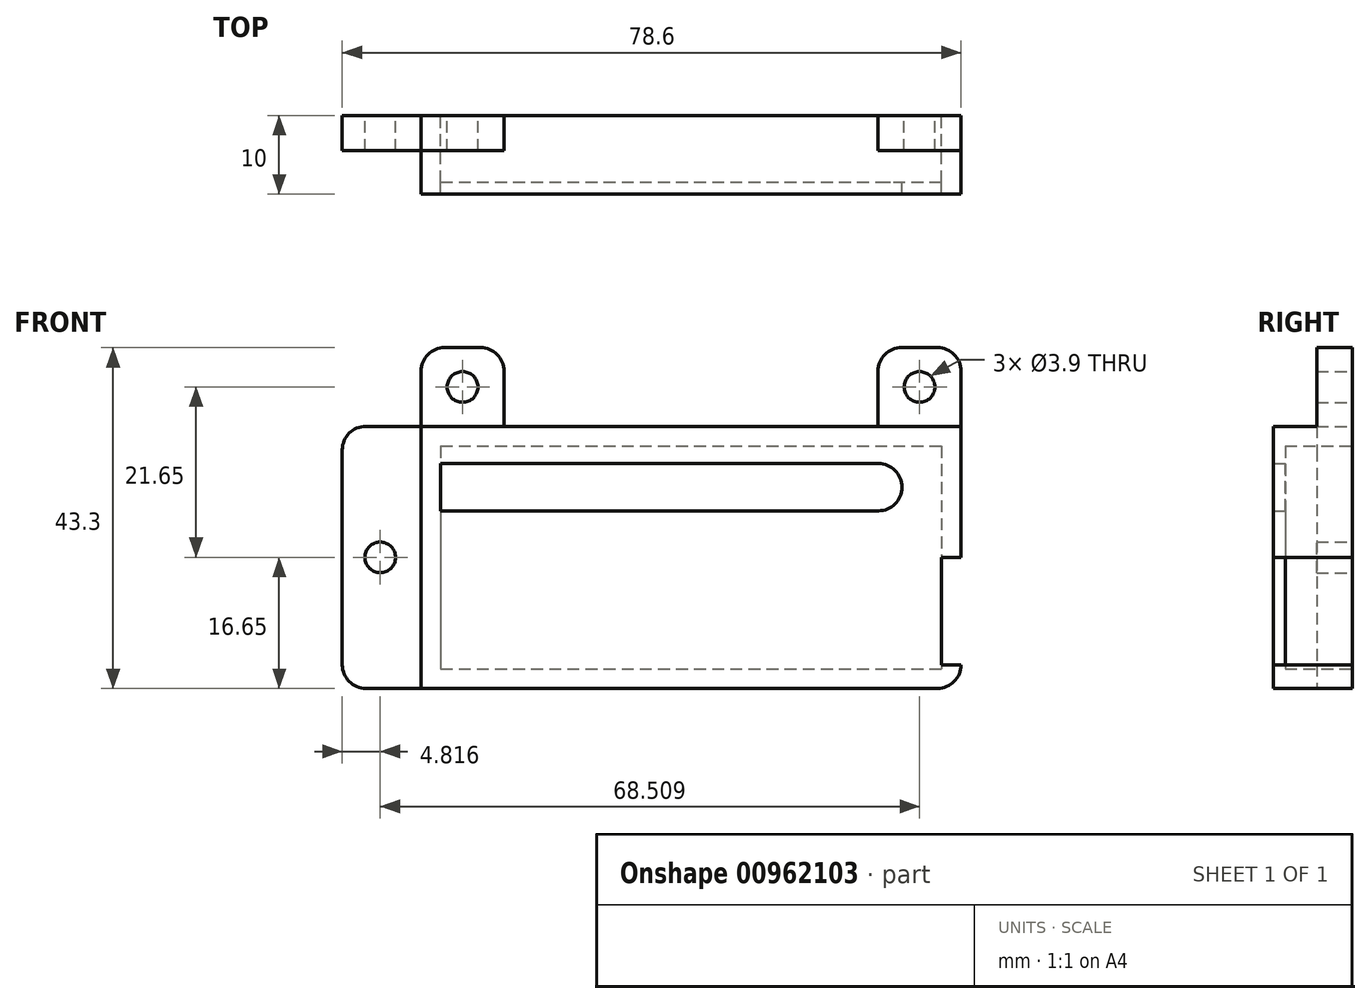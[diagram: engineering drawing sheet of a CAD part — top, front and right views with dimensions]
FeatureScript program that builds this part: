
annotation { "Feature Type Name" : "Feature", "Feature Type Description" : "" }
export const myFeature = defineFeature(function(context is Context, id is Id, definition is map)
    precondition{}
    {
        {
            var Q0;
            Q0=qCreatedBy(makeId("Front.planeOp"),FACE);
            var sketch = newSketch(context, id + "F0", { "sketchPlane" : qUnion([Q0])});
            skLineSegment(sketch, "E0.bottom", {"start": v(-31.8, 14.15) * mm, "end": v(31.8, 14.15) * mm});
            skLineSegment(sketch, "E0.top", {"start": v(-31.8, -14.15) * mm, "end": v(31.8, -14.15) * mm});
            skLineSegment(sketch, "E0.left", {"start": v(-31.8, 14.15) * mm, "end": v(-31.8, -14.15) * mm});
            skLineSegment(sketch, "E0.right", {"start": v(31.8, 14.15) * mm, "end": v(31.8, -14.15) * mm});
            skLineSegment(sketch, "E1", {"start": v(0, 0) * mm, "end": v(0, 14.15) * mm, "construction": true});
            skLineSegment(sketch, "E2", {"start": v(0, 0) * mm, "end": v(0, -14.15) * mm, "construction": true});
            skLineSegment(sketch, "E3", {"start": v(0, 0) * mm, "end": v(31.8, 0) * mm, "construction": true});
            skLineSegment(sketch, "E4", {"start": v(0, 0) * mm, "end": v(-31.8, 0) * mm, "construction": true});
            skLineSegment(sketch, "E5.0", {"start": v(-34.3, 16.65) * mm, "end": v(34.3, 16.65) * mm});
            skLineSegment(sketch, "E5.1", {"start": v(-34.3, 16.65) * mm, "end": v(-34.3, -16.65) * mm});
            skLineSegment(sketch, "E5.2", {"start": v(-34.3, -16.65) * mm, "end": v(31.3, -16.65) * mm});
            skLineSegment(sketch, "E5.3", {"start": v(34.3, 16.65) * mm, "end": v(34.3, 0) * mm});
            skLineSegment(sketch, "E6", {"start": v(23.75, 16.65) * mm, "end": v(23.75, 23.65) * mm});
            skLineSegment(sketch, "E7", {"start": v(26.75, 26.65) * mm, "end": v(31.3, 26.65) * mm});
            skLineSegment(sketch, "E8", {"start": v(34.3, 23.65) * mm, "end": v(34.3, 16.65) * mm});
            skCircle(sketch, "E9", {"center": v(29.02, 21.65) * mm, "radius": 1.95 * mm});
            skLineSegment(sketch, "E10", {"start": v(29.02, 21.65) * mm, "end": v(34.3, 21.65) * mm, "construction": true});
            skLineSegment(sketch, "E11", {"start": v(29.02, 21.65) * mm, "end": v(23.75, 21.65) * mm, "construction": true});
            skLineSegment(sketch, "E12", {"start": v(29.02, 21.65) * mm, "end": v(29.02, 16.65) * mm, "construction": true});
            skLineSegment(sketch, "E13", {"start": v(29.02, 21.65) * mm, "end": v(29.02, 26.65) * mm, "construction": true});
            skLineSegment(sketch, "E14.MirrorCS", {"start": v(-34.3, 23.65) * mm, "end": v(-34.3, 16.65) * mm});
            skLineSegment(sketch, "E15.MirrorCS", {"start": v(-26.75, 26.65) * mm, "end": v(-31.3, 26.65) * mm});
            skLineSegment(sketch, "E16.MirrorCS", {"start": v(-23.75, 16.65) * mm, "end": v(-23.75, 23.65) * mm});
            skCircle(sketch, "E17.MirrorC", {"center": v(-29.02, 21.65) * mm, "radius": 1.95 * mm});
            skLineSegment(sketch, "E18", {"start": v(-34.3, 16.65) * mm, "end": v(-41.3, 16.65) * mm});
            skLineSegment(sketch, "E19", {"start": v(-44.3, 13.65) * mm, "end": v(-44.3, -13.65) * mm});
            skLineSegment(sketch, "E20", {"start": v(-41.3, -16.65) * mm, "end": v(-34.3, -16.65) * mm});
            skCircle(sketch, "E21", {"center": v(-39.48, 0) * mm, "radius": 1.95 * mm});
            skLineSegment(sketch, "E22", {"start": v(34.3, 16.65) * mm, "end": v(41.3, 16.65) * mm});
            skLineSegment(sketch, "E23", {"start": v(44.3, 13.65) * mm, "end": v(44.3, 9.1) * mm});
            skLineSegment(sketch, "E24", {"start": v(41.3, 6.1) * mm, "end": v(34.3, 6.1) * mm});
            skCircle(sketch, "E25", {"center": v(39.3, 11.38) * mm, "radius": 1.95 * mm});
            skLineSegment(sketch, "E26", {"start": v(39.3, 11.38) * mm, "end": v(39.3, 16.65) * mm, "construction": true});
            skLineSegment(sketch, "E27", {"start": v(39.3, 11.38) * mm, "end": v(39.3, 6.1) * mm, "construction": true});
            skLineSegment(sketch, "E28", {"start": v(39.3, 11.38) * mm, "end": v(44.3, 11.38) * mm, "construction": true});
            skLineSegment(sketch, "E29", {"start": v(39.3, 11.38) * mm, "end": v(34.3, 11.38) * mm, "construction": true});
            skLineSegment(sketch, "E30", {"start": v(-31.8, 8.9) * mm, "end": v(23.8, 8.9) * mm, "construction": true});
            skArc(sketch, "E31.0.endCap", {"start": v(23.8, 11.9) * mm, "mid": v(26.8, 8.9) * mm, "end": v(23.8, 5.9) * mm});
            skLineSegment(sketch, "E31.0.left", {"start": v(-31.8, 11.9) * mm, "end": v(23.8, 11.9) * mm});
            skLineSegment(sketch, "E31.0.right", {"start": v(-31.8, 5.9) * mm, "end": v(23.8, 5.9) * mm});
            skLineSegment(sketch, "E32", {"start": v(-31.8, 2.85) * mm, "end": v(31.8, 2.85) * mm, "construction": true});
            skPoint(sketch, "E33.visualSharp", {"position": v(-23.75, 26.65) * mm});
            skArc(sketch, "E33.filletArc", {"start": v(-23.75, 23.65) * mm, "mid": v(-24.63, 25.77) * mm, "end": v(-26.75, 26.65) * mm});
            skPoint(sketch, "E34.visualSharp", {"position": v(-34.3, 26.65) * mm});
            skArc(sketch, "E34.filletArc", {"start": v(-31.3, 26.65) * mm, "mid": v(-33.42, 25.77) * mm, "end": v(-34.3, 23.65) * mm});
            skPoint(sketch, "E35.visualSharp", {"position": v(34.3, 26.65) * mm});
            skArc(sketch, "E35.filletArc", {"start": v(34.3, 23.65) * mm, "mid": v(33.42, 25.77) * mm, "end": v(31.3, 26.65) * mm});
            skPoint(sketch, "E36.visualSharp", {"position": v(23.75, 26.65) * mm});
            skArc(sketch, "E36.filletArc", {"start": v(26.75, 26.65) * mm, "mid": v(24.63, 25.77) * mm, "end": v(23.75, 23.65) * mm});
            skPoint(sketch, "E37.visualSharp", {"position": v(44.3, 16.65) * mm});
            skArc(sketch, "E37.filletArc", {"start": v(44.3, 13.65) * mm, "mid": v(43.42, 15.77) * mm, "end": v(41.3, 16.65) * mm});
            skPoint(sketch, "E38.visualSharp", {"position": v(44.3, 6.1) * mm});
            skArc(sketch, "E38.filletArc", {"start": v(41.3, 6.1) * mm, "mid": v(43.42, 6.98) * mm, "end": v(44.3, 9.1) * mm});
            skPoint(sketch, "E39.visualSharp", {"position": v(-44.3, 16.65) * mm});
            skArc(sketch, "E39.filletArc", {"start": v(-41.3, 16.65) * mm, "mid": v(-43.42, 15.77) * mm, "end": v(-44.3, 13.65) * mm});
            skPoint(sketch, "E40.visualSharp", {"position": v(-44.3, -16.65) * mm});
            skArc(sketch, "E40.filletArc", {"start": v(-44.3, -13.65) * mm, "mid": v(-43.42, -15.77) * mm, "end": v(-41.3, -16.65) * mm});
            skPoint(sketch, "E41.visualSharp", {"position": v(34.3, -16.65) * mm});
            skArc(sketch, "E41.filletArc", {"start": v(31.3, -16.65) * mm, "mid": v(33.42, -15.77) * mm, "end": v(34.3, -13.65) * mm});
            skLineSegment(sketch, "E42", {"start": v(31.8, 0) * mm, "end": v(34.3, 0) * mm});
            skLineSegment(sketch, "E43", {"start": v(34.3, -13.65) * mm, "end": v(31.8, -13.65) * mm});
            skSolve(sketch);
        }
        {
            var Q0;
            {var subQ1=sQuery(id+"F0.wireOp",EDGE,"E14.MirrorCS");Q0=makeQuery(id+"F0.imprint","IMPRINT",FACE,{"disambiguationData":[TD([[makeQuery(id+"F0.imprint","IMPRINT",EDGE,{"derivedFrom":subQ1}),1.0]])]});}
            var Q1;
            {var subQ1=sQuery(id+"F0.wireOp",EDGE,"E6");Q1=makeQuery(id+"F0.imprint","IMPRINT",FACE,{"disambiguationData":[TD([[makeQuery(id+"F0.imprint","IMPRINT",EDGE,{"derivedFrom":subQ1}),-1.0]])]});}
            var Q2;
            {var subQ1=sQuery(id+"F0.wireOp",EDGE,"E22");Q2=makeQuery(id+"F0.imprint","IMPRINT",FACE,{"disambiguationData":[TD([[makeQuery(id+"F0.imprint","IMPRINT",EDGE,{"derivedFrom":subQ1}),-1.0]])]});}
            var Q3;
            {var subQ9=sQuery(id+"F0.wireOp",EDGE,"E0.bottom");Q3=makeQuery(id+"F0.imprint","IMPRINT",FACE,{"disambiguationData":[TD([[makeQuery(id+"F0.imprint","IMPRINT",EDGE,{"derivedFrom":subQ9}),1.0]])]});}
            var Q4;
            Q4=makeQuery(id+"F0.imprint","IMPRINT",FACE,{"disambiguationData":[TD([[makeQuery(id+"F0.imprint","IMPRINT",EDGE,{"derivedFrom":sQuery(id+"F0.wireOp",EDGE,"E5.1")}),-1.0]])]});
            var Q5;
            {var subQ3=sQuery(id+"F0.wireOp",EDGE,"E0.bottom");Q5=makeQuery(id+"F0.imprint","IMPRINT",FACE,{"disambiguationData":[TD([[makeQuery(id+"F0.imprint","IMPRINT",EDGE,{"derivedFrom":subQ3}),-1.0]])]});}
            extrude(context, id + "F1", {"entities" : qUnion([Q0, Q1, Q2, Q3, Q4, Q5]), "depth" : 10 * mm, "offsetDistance" : 25 * mm});
        }
        {
            var Q0;
            {var subQ3=sQuery(id+"F0.wireOp",EDGE,"E0.bottom");Q0=makeQuery(id+"F0.imprint","IMPRINT",FACE,{"disambiguationData":[TD([[makeQuery(id+"F0.imprint","IMPRINT",EDGE,{"derivedFrom":subQ3}),-1.0]])]});}
            extrude(context, id + "F2", {"entities" : qUnion([Q0]), "operationType" : NewBodyOperationType.REMOVE, "depth" : 8.5 * mm, "offsetDistance" : 25 * mm});
        }
        {
            var Q0;
            Q0=makeQuery(id+"F1.opExtrude","CAP_FACE",FACE,{"disambiguationData":[OSD([sQuery(id+"F0.wireOp",EDGE,"E0.left"),sQuery(id+"F0.wireOp",EDGE,"E0.right"),sQuery(id+"F0.wireOp",EDGE,"E5.0"),sQuery(id+"F0.wireOp",EDGE,"E5.2"),sQuery(id+"F0.wireOp",EDGE,"E5.3"),sQuery(id+"F0.wireOp",EDGE,"E6"),sQuery(id+"F0.wireOp",EDGE,"E7"),sQuery(id+"F0.wireOp",EDGE,"E8"),sQuery(id+"F0.wireOp",EDGE,"E9"),sQuery(id+"F0.wireOp",EDGE,"E14.MirrorCS"),sQuery(id+"F0.wireOp",EDGE,"E15.MirrorCS"),sQuery(id+"F0.wireOp",EDGE,"E16.MirrorCS"),sQuery(id+"F0.wireOp",EDGE,"E17.MirrorC"),sQuery(id+"F0.wireOp",EDGE,"E18"),sQuery(id+"F0.wireOp",EDGE,"E19"),sQuery(id+"F0.wireOp",EDGE,"E20"),sQuery(id+"F0.wireOp",EDGE,"E21"),sQuery(id+"F0.wireOp",EDGE,"E22"),sQuery(id+"F0.wireOp",EDGE,"E23"),sQuery(id+"F0.wireOp",EDGE,"E24"),sQuery(id+"F0.wireOp",EDGE,"E25"),sQuery(id+"F0.wireOp",EDGE,"E31.0.endCap"),sQuery(id+"F0.wireOp",EDGE,"E31.0.left"),sQuery(id+"F0.wireOp",EDGE,"E31.0.right"),sQuery(id+"F0.wireOp",EDGE,"E33.filletArc"),sQuery(id+"F0.wireOp",EDGE,"E34.filletArc"),sQuery(id+"F0.wireOp",EDGE,"E35.filletArc"),sQuery(id+"F0.wireOp",EDGE,"E36.filletArc"),sQuery(id+"F0.wireOp",EDGE,"E37.filletArc"),sQuery(id+"F0.wireOp",EDGE,"E38.filletArc"),sQuery(id+"F0.wireOp",EDGE,"E39.filletArc"),sQuery(id+"F0.wireOp",EDGE,"E40.filletArc"),sQuery(id+"F0.wireOp",EDGE,"E41.filletArc"),sQuery(id+"F0.wireOp",EDGE,"E42"),sQuery(id+"F0.wireOp",EDGE,"E43")])],"isStart":false});
            var sketch = newSketch(context, id + "F3", { "sketchPlane" : qUnion([Q0])});
            skLineSegment(sketch, "E44.0.0", {"start": v(-34.3, 23.65) * mm, "end": v(-34.3, 16.65) * mm});
            skLineSegment(sketch, "E44.0.1", {"start": v(-34.3, 16.65) * mm, "end": v(-41.3, 16.65) * mm});
            skArc(sketch, "E44.0.2", {"start": v(-41.3, 16.65) * mm, "mid": v(-43.42, 15.77) * mm, "end": v(-44.3, 13.65) * mm});
            skLineSegment(sketch, "E44.0.3", {"start": v(-44.3, 13.65) * mm, "end": v(-44.3, -13.65) * mm});
            skArc(sketch, "E44.0.4", {"start": v(-44.3, -13.65) * mm, "mid": v(-43.42, -15.77) * mm, "end": v(-41.3, -16.65) * mm});
            skLineSegment(sketch, "E44.0.5", {"start": v(-41.3, -16.65) * mm, "end": v(31.3, -16.65) * mm});
            skArc(sketch, "E44.0.6", {"start": v(31.3, -16.65) * mm, "mid": v(33.42, -15.77) * mm, "end": v(34.3, -13.65) * mm});
            skLineSegment(sketch, "E44.0.7", {"start": v(34.3, -13.65) * mm, "end": v(31.8, -13.65) * mm});
            skLineSegment(sketch, "E44.0.8", {"start": v(31.8, -13.65) * mm, "end": v(31.8, 0) * mm});
            skLineSegment(sketch, "E44.0.9", {"start": v(31.8, 0) * mm, "end": v(34.3, 0) * mm});
            skLineSegment(sketch, "E44.0.10", {"start": v(34.3, 0) * mm, "end": v(34.3, 6.1) * mm});
            skLineSegment(sketch, "E44.0.11", {"start": v(34.3, 6.1) * mm, "end": v(41.3, 6.1) * mm});
            skArc(sketch, "E44.0.12", {"start": v(41.3, 6.1) * mm, "mid": v(43.42, 6.98) * mm, "end": v(44.3, 9.1) * mm});
            skLineSegment(sketch, "E44.0.13", {"start": v(44.3, 9.1) * mm, "end": v(44.3, 13.65) * mm});
            skArc(sketch, "E44.0.14", {"start": v(44.3, 13.65) * mm, "mid": v(43.42, 15.77) * mm, "end": v(41.3, 16.65) * mm});
            skLineSegment(sketch, "E44.0.15", {"start": v(41.3, 16.65) * mm, "end": v(34.3, 16.65) * mm});
            skLineSegment(sketch, "E44.0.16", {"start": v(34.3, 16.65) * mm, "end": v(34.3, 23.65) * mm});
            skArc(sketch, "E44.0.17", {"start": v(34.3, 23.65) * mm, "mid": v(33.42, 25.77) * mm, "end": v(31.3, 26.65) * mm});
            skLineSegment(sketch, "E44.0.18", {"start": v(31.3, 26.65) * mm, "end": v(26.75, 26.65) * mm});
            skArc(sketch, "E44.0.19", {"start": v(26.75, 26.65) * mm, "mid": v(24.63, 25.77) * mm, "end": v(23.75, 23.65) * mm});
            skLineSegment(sketch, "E44.0.20", {"start": v(23.75, 23.65) * mm, "end": v(23.75, 16.65) * mm});
            skLineSegment(sketch, "E44.0.21", {"start": v(23.75, 16.65) * mm, "end": v(-23.75, 16.65) * mm});
            skLineSegment(sketch, "E44.0.22", {"start": v(-23.75, 16.65) * mm, "end": v(-23.75, 23.65) * mm});
            skArc(sketch, "E44.0.23", {"start": v(-23.75, 23.65) * mm, "mid": v(-24.63, 25.77) * mm, "end": v(-26.75, 26.65) * mm});
            skLineSegment(sketch, "E44.0.24", {"start": v(-26.75, 26.65) * mm, "end": v(-31.3, 26.65) * mm});
            skArc(sketch, "E44.0.25", {"start": v(-31.3, 26.65) * mm, "mid": v(-33.42, 25.77) * mm, "end": v(-34.3, 23.65) * mm});
            skLineSegment(sketch, "E45.0", {"start": v(-34.3, 16.65) * mm, "end": v(-34.3, -16.65) * mm});
            skLineSegment(sketch, "E46.0", {"start": v(-34.3, 16.65) * mm, "end": v(34.3, 16.65) * mm});
            skLineSegment(sketch, "E47.0", {"start": v(34.3, 16.65) * mm, "end": v(34.3, 0) * mm});
            skSolve(sketch);
        }
        {
            var Q0;
            {var subQ0=sQuery(id+"F3.wireOp",EDGE,"E44.0.0");Q0=makeQuery(id+"F3.imprint","IMPRINT",FACE,{"disambiguationData":[TD([[makeQuery(id+"F3.imprint","IMPRINT",EDGE,{"derivedFrom":subQ0}),1.0]])]});}
            var Q1;
            Q1=makeQuery(id+"F3.imprint","IMPRINT",FACE,{"disambiguationData":[TD([[makeQuery(id+"F3.imprint","IMPRINT",EDGE,{"derivedFrom":sQuery(id+"F3.wireOp",EDGE,"E44.0.1")}),1.0]])]});
            var Q2;
            {var subQ1=sQuery(id+"F3.wireOp",EDGE,"E44.0.16");Q2=makeQuery(id+"F3.imprint","IMPRINT",FACE,{"disambiguationData":[TD([[makeQuery(id+"F3.imprint","IMPRINT",EDGE,{"derivedFrom":subQ1}),-1.0]])]});}
            var Q3;
            {var subQ0=sQuery(id+"F3.wireOp",EDGE,"E44.0.11");Q3=makeQuery(id+"F3.imprint","IMPRINT",FACE,{"disambiguationData":[TD([[makeQuery(id+"F3.imprint","IMPRINT",EDGE,{"derivedFrom":subQ0}),-1.0]])]});}
            extrude(context, id + "F4", {"entities" : qUnion([Q0, Q1, Q2, Q3]), "operationType" : NewBodyOperationType.REMOVE, "oppositeDirection" : true, "depth" : 5.5 * mm, "offsetDistance" : 25 * mm});
        }
        {
            var Q0;
            {var subQ9=sQuery(id+"F0.wireOp",EDGE,"E0.bottom");Q0=makeQuery(id+"F0.imprint","IMPRINT",FACE,{"disambiguationData":[TD([[makeQuery(id+"F0.imprint","IMPRINT",EDGE,{"derivedFrom":subQ9}),1.0]])]});}
            var sketch = newSketch(context, id + "F5", { "sketchPlane" : qUnion([Q0])});
            skLineSegment(sketch, "E48.0", {"start": v(34.3, 23.65) * mm, "end": v(34.3, 16.65) * mm});
            skLineSegment(sketch, "E49.0", {"start": v(34.3, 16.65) * mm, "end": v(34.3, 0) * mm});
            skLineSegment(sketch, "E50", {"start": v(34.3, 23.65) * mm, "end": v(52.1, 24.63) * mm});
            skLineSegment(sketch, "E51", {"start": v(52.1, 24.63) * mm, "end": v(53.58, -2.36) * mm});
            skLineSegment(sketch, "E52", {"start": v(53.58, -2.36) * mm, "end": v(34.3, 0) * mm});
            skSolve(sketch);
        }
        {
            var Q0;
            Q0 = qSketchRegion(id + "F5", true);
            extrude(context, id + "F6", {"entities" : qUnion([Q0]), "operationType" : NewBodyOperationType.REMOVE, "depth" : 25 * mm, "offsetDistance" : 25 * mm});
        }
    });
